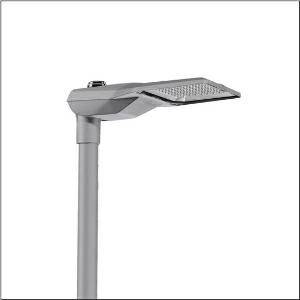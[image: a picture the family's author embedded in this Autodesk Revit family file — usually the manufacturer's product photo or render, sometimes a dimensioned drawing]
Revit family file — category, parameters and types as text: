
# Revit family: streetlight_sl_21_midi___pl52_5xe7h37n08lb_6d16
name_source: partatom
category: Lighting Fixtures
units: mm (PartAtom-declared; Revit-internal decimal feet)

## family parameters
Cut with Voids When Loaded = No
Host = Face
Light Source = No
Part Type = Normal
Room Calculation Point = No
Round Connector Dimension = Use Diameter
Shared = No

## types (1)
- --- (1 x LED, 14100 lm, 98.3 W, 3000K)
    Apparent Load = 98 VA
    CIE Flux Codes = 27 59 98 100 100
    Color Rendering = 70
    Color Temperature = 3000K
    Default Elevation = 1800 mm
    Description = Streetlight SL 21 midi, mast luminaire, primary light control with lens, of PMMA, primary optical cover: cover, of toughened safety glass, transparent, light distribution: PL52, light emission: direct distribution, primary light characteristic: asymmetric, installation type: side-entry, LED, 3G 2.5mm², High Power LED, rated luminous flux: 14.100lm, luminous efficacy: 143lm/W, light colour: 730, colour temperature: 3000K, control: overheat protection, presetting dimming linear, constant luminous flux control, time-dependent luminous flux control, flexible luminous flux parameterisation, mains connection: 220..240V, AC, 50/60Hz, connection cable pre-assembled, cable length: 10,5m, wiring characteristics: H05VV-F, start of lifetime: 98W, end of service life: 101W, reduction: 45W, luminaire housing, of diecast aluminium (EN AC-44300), powder-coated, Siteco® metallic grey (DB 702S), corrosivity category C5 mid according to DIN EN ISO 12944, multi-level sealing system, sealing non-destructively replaceable, inclination adjustable: 0°, 5°, 10°, 15°, length: 644mm, width: 335mm, height: 110mm, spigot size: 42mm (side-entry), protection rating (complete): IP66, insulation class (complete): insulation class I (protective earthing), certification: CE, ENEC, ENEC+, VDE, impact resistance: IK09, permissible operating ambient temperature for outdoor applications: -40..+50°C, standard-compliant lighting for roads and squares, packaging unit: 1 piece

Light Distribution: PL52
    Height = 111 mm
    Lamp = 1 x LED
    Lamp Light Flux = 14100 lm
    Lamp Power = 98.3 W
    Lamp count = 1
    Length = 644 mm
    Luminous efficacy = 143 lm/W
    Manufacturer = Siteco
    ModVariant = No
    Model = 5XE7H37N08LB
    Number of Poles = 1
    OnlyDefault = Yes
    Power Factor = 1
    Product Name = Streetlight SL 21 midi | PL52
    Product group = mast luminaire | pylon top
    ProductGroupID = 6100
    Protection Class = Protection class I
    Protection Degree = IP 66
    RLX_Detail_Level = 1
    RLX_Emergency_Light_Flux = 0 lm
    RLX_Emergency_Type = 0
    RLX_Emergency_Type_DB = No
    RlxData = <blob elided: 100185 chars, md5=7405ada2>
    Socket = socket
    Standby Power = 0 W
    System Light Flux = 14100 lm
    System Power = 98 W
    Type Comments = factory setting: luminous flux: 100 % | dim-lin: 254 | 1020 mA
    Type Image = l_1294377.jpg
    URL = http://relux.com
    VarID = @adj_086303
    Voltage = 0 V
    Weight = 0.00 kg
    Width = 336 mm

## geometry (parser evidence)
native form markers: Blend x4, Sweep x10
no freeform markers — native parametric forms only
